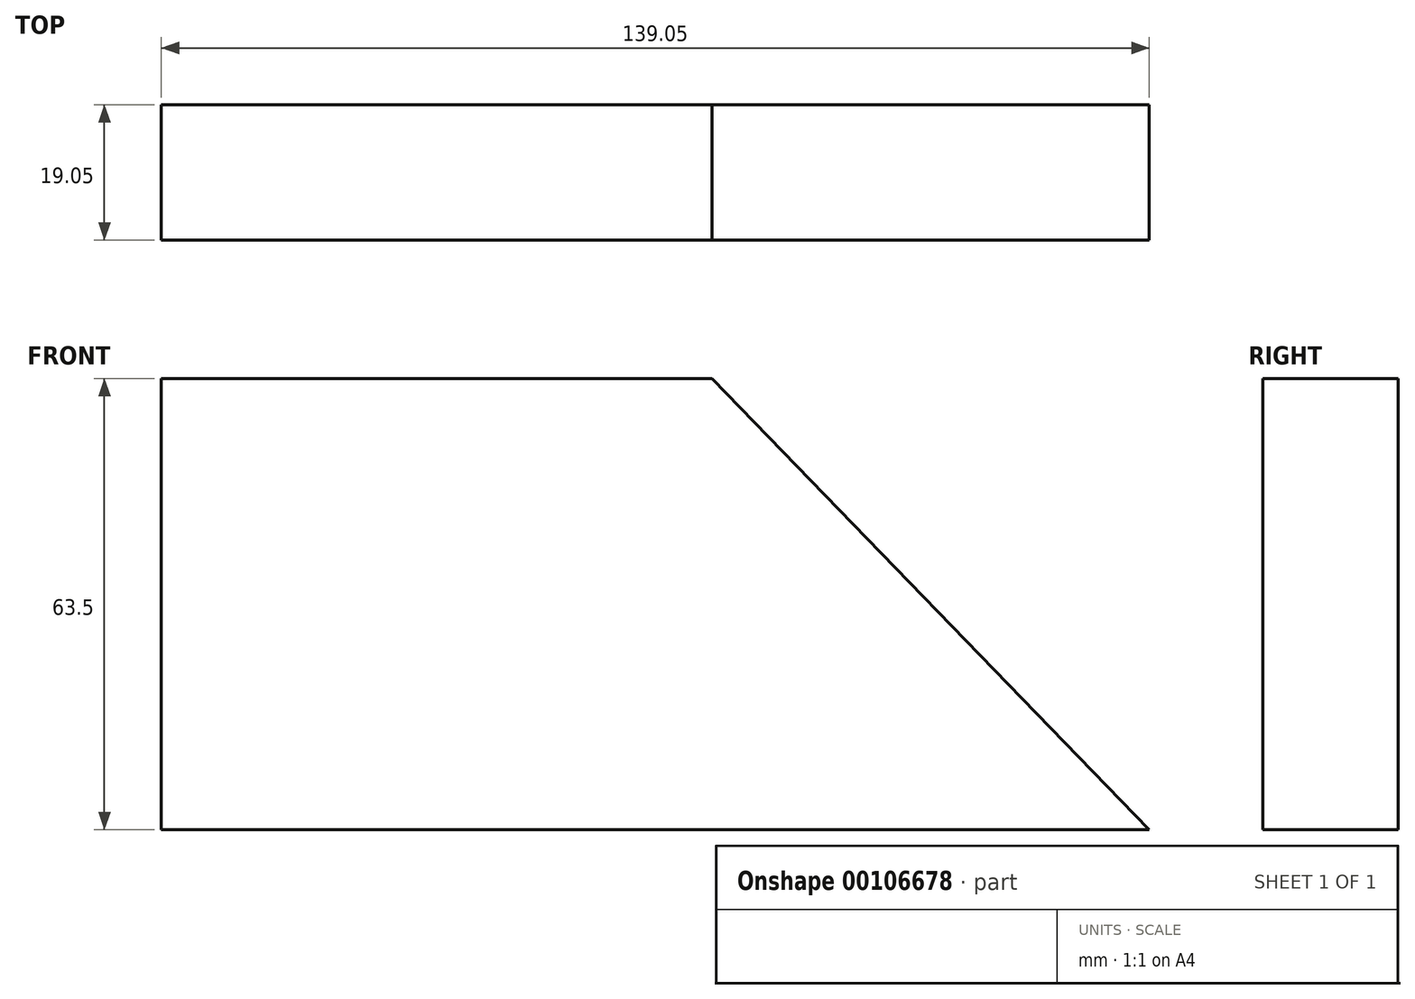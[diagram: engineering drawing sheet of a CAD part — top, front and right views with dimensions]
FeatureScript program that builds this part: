
annotation { "Feature Type Name" : "Feature", "Feature Type Description" : "" }
export const myFeature = defineFeature(function(context is Context, id is Id, definition is map)
    precondition{}
    {
        {
            var Q0;
            Q0=qCreatedBy(makeId("Front.planeOp"),FACE);
            var sketch = newSketch(context, id + "F0", { "sketchPlane" : qUnion([Q0])});
            skLineSegment(sketch, "E0.top", {"start": v(0, 63.5) * mm, "end": v(77.54, 63.5) * mm});
            skLineSegment(sketch, "E0.left", {"start": v(0, 0) * mm, "end": v(0, 63.5) * mm});
            skLineSegment(sketch, "E1", {"start": v(77.54, 63.5) * mm, "end": v(139.05, 0) * mm});
            skLineSegment(sketch, "E2", {"start": v(139.05, 0) * mm, "end": v(0, 0) * mm});
            skSolve(sketch);
        }
        {
            var Q0;
            Q0=makeQuery(id+"F0.imprint","IMPRINT",FACE,{"disambiguationData":[TD([[makeQuery(id+"F0.imprint","IMPRINT",EDGE,{"derivedFrom":sQuery(id+"F0.wireOp",EDGE,"E0.bottom")}),1.0]])]});
            var Q1;
            Q1=makeQuery(id+"F0.imprint","IMPRINT",FACE,{"disambiguationData":[TD([[makeQuery(id+"F0.imprint","IMPRINT",EDGE,{"derivedFrom":sQuery(id+"F0.wireOp",EDGE,"E0.top")}),-1.0]])]});
            extrude(context, id + "F1", {"entities" : qUnion([Q0, Q1]), "depth" : 19.05 * mm});
        }
    });
